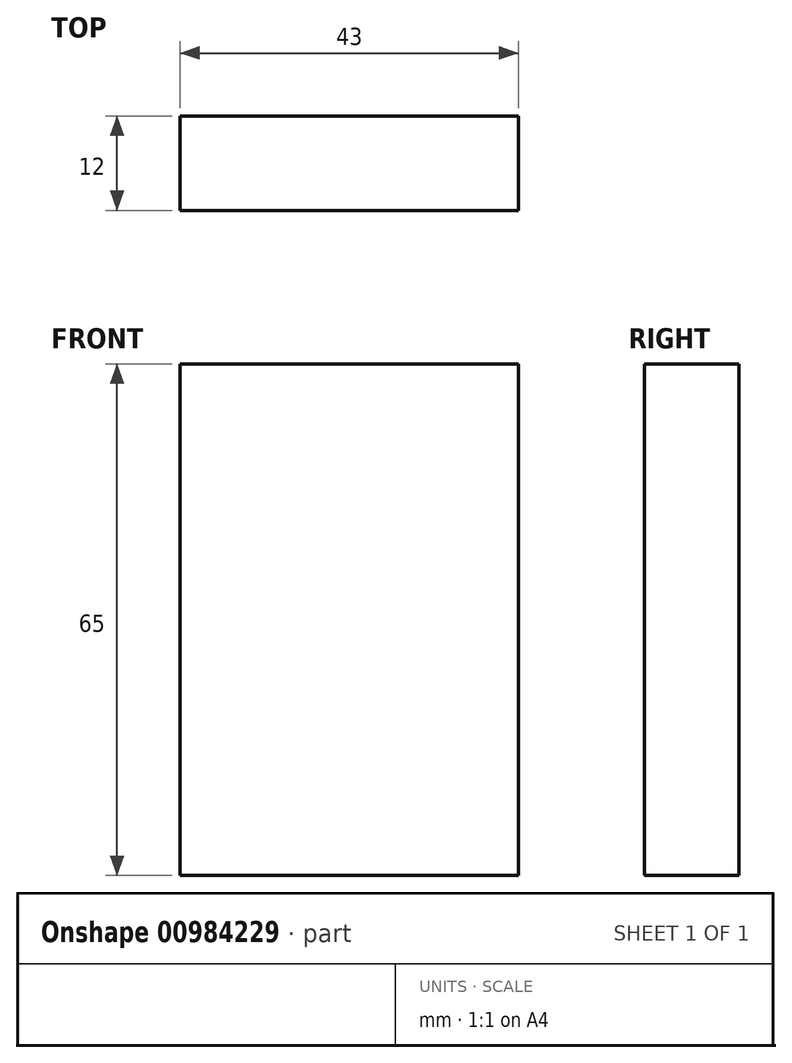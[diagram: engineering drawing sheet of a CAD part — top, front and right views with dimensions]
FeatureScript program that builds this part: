
annotation { "Feature Type Name" : "Feature", "Feature Type Description" : "" }
export const myFeature = defineFeature(function(context is Context, id is Id, definition is map)
    precondition{}
    {
        {
            var Q0;
            Q0=qCreatedBy(makeId("Front.planeOp"),FACE);
            var sketch = newSketch(context, id + "F0", { "sketchPlane" : qUnion([Q0])});
            skLineSegment(sketch, "E0.bottom", {"start": v(21.5, 32.5) * mm, "end": v(-21.5, 32.5) * mm});
            skLineSegment(sketch, "E0.top", {"start": v(21.5, -32.5) * mm, "end": v(-21.5, -32.5) * mm});
            skLineSegment(sketch, "E0.left", {"start": v(21.5, 32.5) * mm, "end": v(21.5, -32.5) * mm});
            skLineSegment(sketch, "E0.right", {"start": v(-21.5, 32.5) * mm, "end": v(-21.5, -32.5) * mm});
            skPoint(sketch, "E0.middle", {"position": v(0, 0) * mm});
            skSolve(sketch);
        }
        {
            var Q0;
            Q0=makeQuery(id+"F0.imprint","IMPRINT",FACE,{"disambiguationData":[TD([[makeQuery(id+"F0.imprint","IMPRINT",EDGE,{"derivedFrom":sQuery(id+"F0.wireOp",EDGE,"E0.bottom")}),1.0]])]});
            extrude(context, id + "F1", {"entities" : qUnion([Q0]), "oppositeDirection" : true, "depth" : 12 * mm, "offsetDistance" : 25 * mm});
        }
    });
